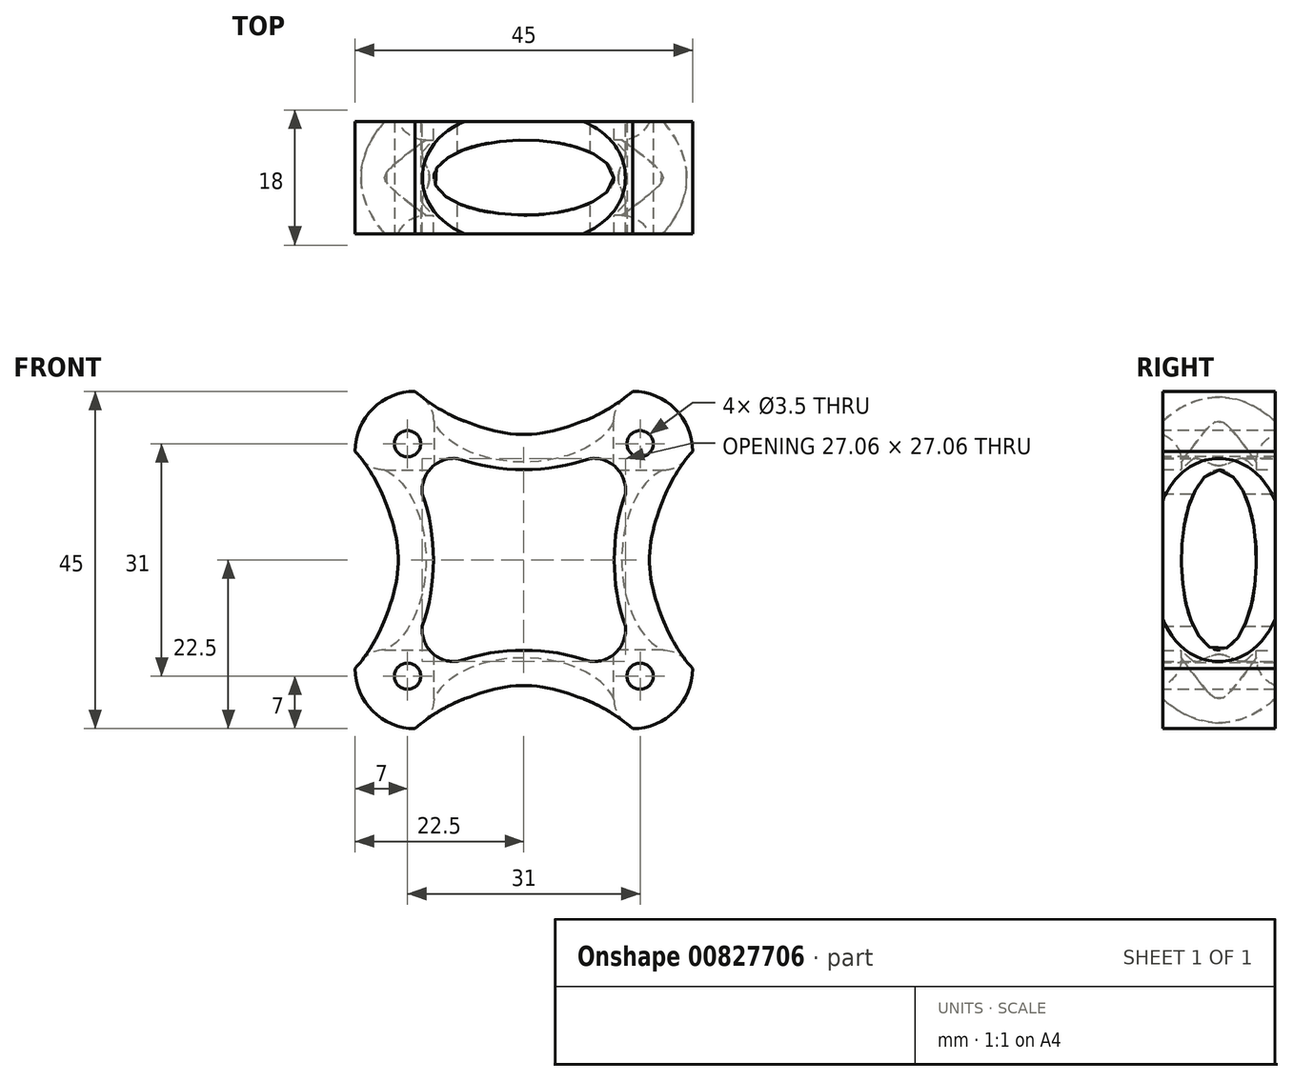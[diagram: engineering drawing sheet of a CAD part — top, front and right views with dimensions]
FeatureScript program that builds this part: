
annotation { "Feature Type Name" : "Feature", "Feature Type Description" : "" }
export const myFeature = defineFeature(function(context is Context, id is Id, definition is map)
    precondition{}
    {
        {
            var Q0;
            Q0=qCreatedBy(makeId("Front.planeOp"),FACE);
            var sketch = newSketch(context, id + "F0", { "sketchPlane" : qUnion([Q0])});
            skLineSegment(sketch, "E0.bottom", {"start": v(-15.5, 15.5) * mm, "end": v(15.5, 15.5) * mm, "construction": true});
            skLineSegment(sketch, "E0.top", {"start": v(-15.5, -15.5) * mm, "end": v(15.5, -15.5) * mm, "construction": true});
            skLineSegment(sketch, "E0.left", {"start": v(-15.5, 15.5) * mm, "end": v(-15.5, -15.5) * mm, "construction": true});
            skLineSegment(sketch, "E0.right", {"start": v(15.5, 15.5) * mm, "end": v(15.5, -15.5) * mm, "construction": true});
            skPoint(sketch, "E0.middle", {"position": v(0, 0) * mm});
            skCircle(sketch, "E1", {"center": v(-15.5, 15.5) * mm, "radius": 2.75 * mm, "construction": true});
            skCircle(sketch, "E2", {"center": v(15.5, 15.5) * mm, "radius": 2.75 * mm, "construction": true});
            skCircle(sketch, "E3", {"center": v(-15.5, -15.5) * mm, "radius": 2.75 * mm, "construction": true});
            skCircle(sketch, "E4", {"center": v(15.5, -15.5) * mm, "radius": 2.75 * mm, "construction": true});
            skCircle(sketch, "E5", {"center": v(0, 0) * mm, "radius": 6.6 * mm});
            skLineSegment(sketch, "E6.bottom", {"start": v(14.5, 22.5) * mm, "end": v(-14.5, 22.5) * mm});
            skLineSegment(sketch, "E6.top", {"start": v(14.5, -22.5) * mm, "end": v(-14.5, -22.5) * mm});
            skLineSegment(sketch, "E6.left", {"start": v(22.5, 14.5) * mm, "end": v(22.5, 0) * mm});
            skLineSegment(sketch, "E6.right", {"start": v(-22.5, 14.5) * mm, "end": v(-22.5, 0) * mm});
            skPoint(sketch, "E7.visualSharp", {"position": v(-22.5, 22.5) * mm});
            skArc(sketch, "E7.filletArc", {"start": v(-14.5, 22.5) * mm, "mid": v(-20.16, 20.16) * mm, "end": v(-22.5, 14.5) * mm});
            skPoint(sketch, "E8.visualSharp", {"position": v(22.5, 22.5) * mm});
            skArc(sketch, "E8.filletArc", {"start": v(22.5, 14.5) * mm, "mid": v(20.16, 20.16) * mm, "end": v(14.5, 22.5) * mm});
            skPoint(sketch, "E9.visualSharp", {"position": v(22.5, -22.5) * mm});
            skArc(sketch, "E9.filletArc", {"start": v(14.5, -22.5) * mm, "mid": v(20.16, -20.16) * mm, "end": v(22.5, -14.5) * mm});
            skPoint(sketch, "E10.visualSharp", {"position": v(-22.5, -22.5) * mm});
            skArc(sketch, "E10.filletArc", {"start": v(-22.5, -14.5) * mm, "mid": v(-20.16, -20.16) * mm, "end": v(-14.5, -22.5) * mm});
            skLineSegment(sketch, "E11", {"start": v(-22.5, 0) * mm, "end": v(-22.5, -14.5) * mm});
            skLineSegment(sketch, "E12", {"start": v(22.5, 0) * mm, "end": v(22.5, -14.5) * mm});
            skArc(sketch, "E13", {"start": v(-22.5, -14.5) * mm, "mid": v(-17.05, 0) * mm, "end": v(-22.5, 14.5) * mm});
            skArc(sketch, "E14", {"start": v(-14.5, 22.5) * mm, "mid": v(0, 17.05) * mm, "end": v(14.5, 22.5) * mm});
            skArc(sketch, "E15", {"start": v(22.5, 14.5) * mm, "mid": v(17.05, 0) * mm, "end": v(22.5, -14.5) * mm});
            skArc(sketch, "E16", {"start": v(14.5, -22.5) * mm, "mid": v(0, -17.05) * mm, "end": v(-14.5, -22.5) * mm});
            skArc(sketch, "E17", {"start": v(-8.83, 13.53) * mm, "mid": v(0, 12.05) * mm, "end": v(8.83, 13.53) * mm});
            skArc(sketch, "E18", {"start": v(-8.83, 13.53) * mm, "mid": v(-12.3, 12.3) * mm, "end": v(-13.53, 8.83) * mm});
            skArc(sketch, "E19.1.0", {"start": v(-13.53, -8.83) * mm, "mid": v(-12.3, -12.3) * mm, "end": v(-8.83, -13.53) * mm});
            skArc(sketch, "E19.2.0", {"start": v(8.83, -13.53) * mm, "mid": v(12.3, -12.3) * mm, "end": v(13.53, -8.83) * mm});
            skArc(sketch, "E19.3.0", {"start": v(13.53, 8.83) * mm, "mid": v(12.3, 12.3) * mm, "end": v(8.83, 13.53) * mm});
            skArc(sketch, "E20", {"start": v(13.53, 8.83) * mm, "mid": v(12.05, 0) * mm, "end": v(13.53, -8.83) * mm});
            skArc(sketch, "E21", {"start": v(8.83, -13.53) * mm, "mid": v(0, -12.05) * mm, "end": v(-8.83, -13.53) * mm});
            skArc(sketch, "E22", {"start": v(-13.53, -8.83) * mm, "mid": v(-12.05, 0) * mm, "end": v(-13.53, 8.83) * mm});
            skSolve(sketch);
        }
        {
            var Q0;
            Q0=makeQuery(id+"F0.imprint","IMPRINT",FACE,{"disambiguationData":[TD([[makeQuery(id+"F0.imprint","IMPRINT",EDGE,{"derivedFrom":sQuery(id+"F0.wireOp",EDGE,"E7.filletArc")}),1.0]])]});
            extrude(context, id + "F1", {"entities" : qUnion([Q0]), "depth" : 15 * mm, "offsetDistance" : 25 * mm});
        }
        {
            var Q0;
            Q0=sQuery(id+"F0.wireOp",VERTEX,"E0.bottom.end");
            var Q1;
            Q1=sQuery(id+"F0.wireOp",VERTEX,"E0.top.end");
            var Q2;
            Q2=sQuery(id+"F0.wireOp",VERTEX,"E0.top.start");
            var Q3;
            Q3=sQuery(id+"F0.wireOp",VERTEX,"E0.bottom.start");
            var Q4;
            Q4=makeQuery(id+"F1.opExtrude","SWEPT_BODY",BODY,{"disambiguationData":[OSD([sQuery(id+"F0.wireOp",EDGE,"E7.filletArc"),sQuery(id+"F0.wireOp",EDGE,"E8.filletArc"),sQuery(id+"F0.wireOp",EDGE,"E9.filletArc"),sQuery(id+"F0.wireOp",EDGE,"E10.filletArc"),sQuery(id+"F0.wireOp",EDGE,"E13"),sQuery(id+"F0.wireOp",EDGE,"E14"),sQuery(id+"F0.wireOp",EDGE,"E15"),sQuery(id+"F0.wireOp",EDGE,"E16"),sQuery(id+"F0.wireOp",EDGE,"E17"),sQuery(id+"F0.wireOp",EDGE,"E18"),sQuery(id+"F0.wireOp",EDGE,"E19.1.0"),sQuery(id+"F0.wireOp",EDGE,"E19.2.0"),sQuery(id+"F0.wireOp",EDGE,"E19.3.0"),sQuery(id+"F0.wireOp",EDGE,"E20"),sQuery(id+"F0.wireOp",EDGE,"E21"),sQuery(id+"F0.wireOp",EDGE,"E22")])]});
            hole(context, id + "F2", {"style" : HoleStyle.SIMPLE, "endStyle" : HoleEndStyle.THROUGH, "oppositeDirection" : true, "holeDiameter" : 3.5 * mm, "majorDiameter" : 5 * mm, "isTappedThrough" : true, "tappedDepth" : 12 * mm, "tapClearance" : 3, "locations" : qUnion([Q0, Q1, Q2, Q3]), "scope" : qUnion([Q4]), "startStyle" : HoleStartStyle.PART});
        }
        {
            var Q0;
            Q0=qCreatedBy(makeId("Right.planeOp"),FACE);
            cPlane(context, id + "F3", {"entities" : qUnion([Q0]), "cplaneType" : CPlaneType.OFFSET, "offset" : 25 * mm, "width" : 150 * mm, "height" : 150 * mm});
        }
        {
            var Q0;
            Q0=qCreatedBy(makeId("Top.planeOp"),FACE);
            cPlane(context, id + "F4", {"entities" : qUnion([Q0]), "cplaneType" : CPlaneType.OFFSET, "offset" : 25 * mm, "width" : 150 * mm, "height" : 150 * mm});
        }
        {
            var Q0;
            Q0=qCreatedBy(id+"F3.planeOp",FACE);
            var sketch = newSketch(context, id + "F5", { "sketchPlane" : qUnion([Q0])});
            skLineSegment(sketch, "E23", {"start": v(0, 0) * mm, "end": v(-15, 0) * mm});
            skEllipse(sketch, "E24", {"center": v(-7.5, 0) * mm, "majorRadius": 12 * mm, "minorRadius": 5 * mm, "majorAxis": v(0, 1)});
            skSolve(sketch);
        }
        {
            var Q0;
            Q0 = qSketchRegion(id + "F5", true);
            extrude(context, id + "F6", {"entities" : qUnion([Q0]), "operationType" : NewBodyOperationType.REMOVE, "oppositeDirection" : true, "depth" : 60 * mm, "offsetDistance" : 25 * mm});
        }
        {
            var Q0;
            Q0=qCreatedBy(id+"F4.planeOp",FACE);
            var sketch = newSketch(context, id + "F7", { "sketchPlane" : qUnion([Q0])});
            skEllipse(sketch, "E25", {"center": v(0, -7.5) * mm, "majorRadius": 12 * mm, "minorRadius": 5 * mm, "majorAxis": v(1, 0)});
            skSolve(sketch);
        }
        {
            var Q0;
            Q0=makeQuery(id+"F7.imprint","IMPRINT",FACE,{"disambiguationData":[TD([[makeQuery(id+"F7.imprint","IMPRINT",EDGE,{"derivedFrom":sQuery(id+"F7.wireOp",EDGE,"E25")}),1.0]])]});
            extrude(context, id + "F8", {"entities" : qUnion([Q0]), "operationType" : NewBodyOperationType.REMOVE, "oppositeDirection" : true, "depth" : 60 * mm, "offsetDistance" : 25 * mm});
        }
        {
            var Q0;
            Q0=makeQuery(id+"F6.boolean.opBoolean","INTERSECT",EDGE,{"derivedFrom":[makeQuery(id+"F1.opExtrude","SWEPT_FACE",FACE,{"disambiguationData":[OSD([sQuery(id+"F0.wireOp",EDGE,"E15")])]}),makeQuery(id+"F6.opExtrude","SWEPT_FACE",FACE,{"disambiguationData":[OSD([sQuery(id+"F5.wireOp",EDGE,"E24")])]})]});
            var Q1;
            Q1=makeQuery(id+"F8.boolean.opBoolean","INTERSECT",EDGE,{"derivedFrom":[makeQuery(id+"F1.opExtrude","SWEPT_FACE",FACE,{"disambiguationData":[OSD([sQuery(id+"F0.wireOp",EDGE,"E16")])]}),makeQuery(id+"F8.opExtrude","SWEPT_FACE",FACE,{"disambiguationData":[OSD([sQuery(id+"F7.wireOp",EDGE,"E25")])]})]});
            var Q2;
            Q2=makeQuery(id+"F6.boolean.opBoolean","INTERSECT",EDGE,{"derivedFrom":[makeQuery(id+"F1.opExtrude","SWEPT_FACE",FACE,{"disambiguationData":[OSD([sQuery(id+"F0.wireOp",EDGE,"E13")])]}),makeQuery(id+"F6.opExtrude","SWEPT_FACE",FACE,{"disambiguationData":[OSD([sQuery(id+"F5.wireOp",EDGE,"E24")])]})]});
            var Q3;
            Q3=makeQuery(id+"F8.boolean.opBoolean","INTERSECT",EDGE,{"derivedFrom":[makeQuery(id+"F1.opExtrude","SWEPT_FACE",FACE,{"disambiguationData":[OSD([sQuery(id+"F0.wireOp",EDGE,"E14")])]}),makeQuery(id+"F8.opExtrude","SWEPT_FACE",FACE,{"disambiguationData":[OSD([sQuery(id+"F7.wireOp",EDGE,"E25")])]})]});
            fillet(context, id + "F9", {"entities" : qUnion([Q0, Q1, Q2, Q3]), "radius" : 4 * mm, "tangentPropagation" : true, "allowEdgeOverflow" : false});
        }
    });
